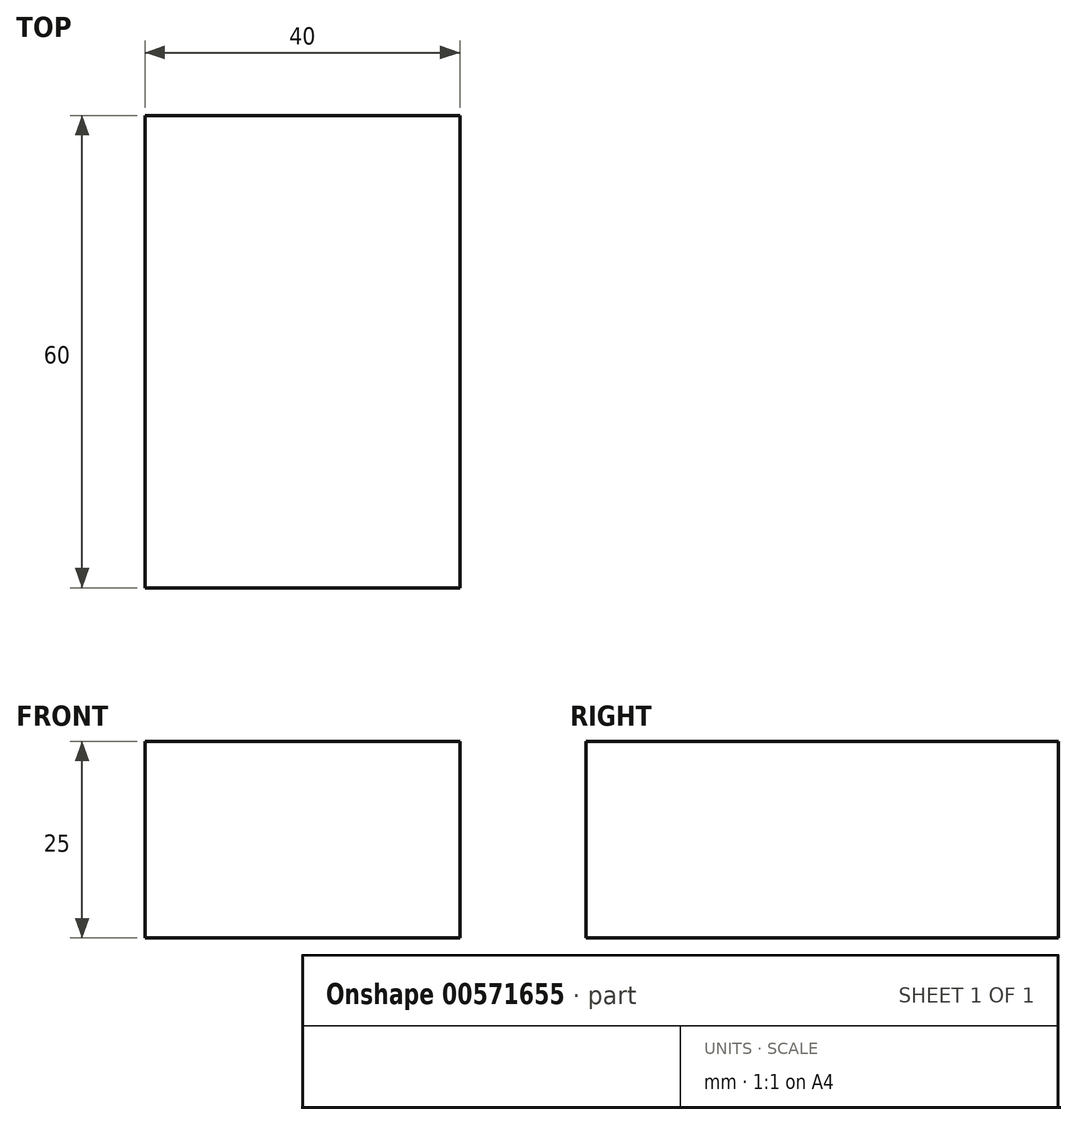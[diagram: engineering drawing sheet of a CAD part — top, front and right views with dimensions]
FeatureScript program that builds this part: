
annotation { "Feature Type Name" : "Feature", "Feature Type Description" : "" }
export const myFeature = defineFeature(function(context is Context, id is Id, definition is map)
    precondition{}
    {
        {
            var Q0;
            Q0=qCreatedBy(makeId("Top.planeOp"),FACE);
            var sketch = newSketch(context, id + "F0", { "sketchPlane" : qUnion([Q0])});
            skLineSegment(sketch, "E0", {"start": v(0, 0) * mm, "end": v(40, 0) * mm});
            skLineSegment(sketch, "E1", {"start": v(40, 0) * mm, "end": v(40, 60) * mm});
            skLineSegment(sketch, "E2", {"start": v(40, 60) * mm, "end": v(0, 60) * mm});
            skLineSegment(sketch, "E3", {"start": v(0, 60) * mm, "end": v(0, 0) * mm});
            skSolve(sketch);
        }
        {
            var Q0;
            Q0=makeQuery(id+"F0.imprint","IMPRINT",FACE,{"disambiguationData":[TD([[makeQuery(id+"F0.imprint","IMPRINT",EDGE,{"derivedFrom":sQuery(id+"F0.wireOp",EDGE,"E0")}),1.0]])]});
            extrude(context, id + "F1", {"entities" : qUnion([Q0]), "depth" : 25 * mm, "offsetDistance" : 25 * mm});
        }
    });
